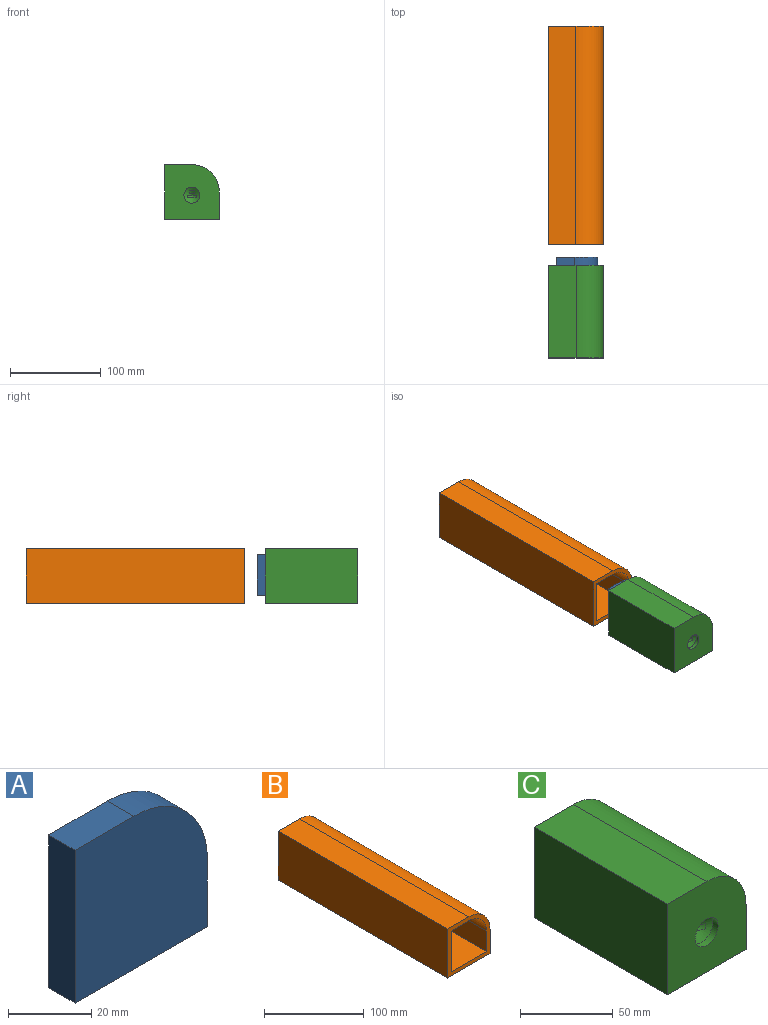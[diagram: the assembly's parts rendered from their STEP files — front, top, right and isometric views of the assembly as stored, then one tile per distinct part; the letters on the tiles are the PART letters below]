
ASSEMBLY  parts=3 mates=2
PART A: 7 faces, bbox 45x9x45 mm
  f0: plane 45x9mm, normal (-1,0,0), area 405mm2, adj f1,f4,f5,f6
  f1: plane 45x9mm, normal (0,0,-1), area 405mm2, adj f0,f2,f5,f6
  f2: plane 20x9mm, normal (1,0,0), area 180mm2, adj f1,f3,f5,f6
  f3: cylinder r=25mm len=25mm, axis (0,1,0), area 353.4mm2, adj f2,f4,f5,f6
  f4: plane 20x9mm, normal (0,0,1), area 180mm2, adj f0,f3,f5,f6
  f5: plane 45x45mm, normal (0,-1,0), area 1890.9mm2, adj f0,f1,f2,f3,f4
  f6: plane 45x45mm, normal (0,1,0), area 1890.9mm2, adj f0,f1,f2,f3,f4
PART B: 13 faces, bbox 60x240x60 mm
  f0: plane 60x60mm, normal (0,-1,0), area 1041mm2, adj f1,f2,f3,f4,f5,f7,f8,f9
  f1: plane 240x60mm, normal (-1,0,0), area 14400mm2, adj f0,f2,f5,f6
  f2: plane 240x60mm, normal (0,0,-1), area 14400mm2, adj f0,f1,f3,f6
  f3: plane 240x30mm, normal (1,0,0), area 7200mm2, adj f0,f2,f4,f6
  f4: cylinder r=30mm len=240mm, axis (0,1,0), area 11309.7mm2, adj f0,f3,f5,f6
  f5: plane 240x30mm, normal (0,0,1), area 7200mm2, adj f0,f1,f4,f6
  f6: plane 60x60mm, normal (0,1,0), area 3406.9mm2, adj f1,f2,f3,f4,f5
  f7: plane 235x50mm, normal (1,0,0), area 11750mm2, adj f0,f8,f11,f12
  f8: plane 235x50mm, normal (0,0,1), area 11750mm2, adj f0,f7,f9,f12
  f9: plane 235x25mm, normal (-1,0,0), area 5875mm2, adj f0,f8,f10,f12
  f10: cylinder r=25mm len=235mm, axis (0,1,0), area 9228.4mm2, adj f0,f9,f11,f12
  f11: plane 235x25mm, normal (0,0,-1), area 5875mm2, adj f0,f7,f10,f12
  f12: plane 50x50mm, normal (0,-1,0), area 2365.9mm2, adj f7,f8,f9,f10,f11
PART C: 19 faces, bbox 60x102x60 mm
  f0: plane 96.01x5mm, normal (0,0,-1), area 478.7mm2, adj f1,f3,f17,f18
  f1: plane 96.01x2.7mm, normal (-0.98,0,-0.18), area 261.9mm2, adj f0,f2,f3,f18
  f2: plane 94.99x6mm, normal (0,0,1), area 566.1mm2, adj f1,f3,f17,f18
  f3: plane 60x60mm, normal (0,1,0), area 3360.8mm2, adj f0,f1,f2,f4,f6,f7,f8,f9
  f4: plane 95.76x10.04mm, normal (0,0,-1), area 946.1mm2, adj f3,f5,f6,f8
  f5: cone r=0mm half-angle=59deg, axis (0,-1,0), area 36.4mm2, adj f4,f6,f7,f8
  f6: plane 96.29x3.11mm, normal (-1,0,0), area 298.1mm2, adj f3,f4,f5,f7
  f7: plane 96.29x10.04mm, normal (0,0,1), area 956.1mm2, adj f3,f5,f6,f8
  f8: plane 96.29x3.11mm, normal (1,0,0), area 298.1mm2, adj f3,f4,f5,f7
  f9: plane 102x60mm, normal (0,0,-1), area 6120mm2, adj f3,f10,f13,f16
  f10: plane 60x60mm, normal (0,-1,0), area 3166.3mm2, adj f9,f11,f13,f14,f15,f16
  f11: cylinder r=8.75mm len=17.5mm, axis (0,-1,0), area 219.9mm2, adj f10,f12
  f12: cone r=0mm half-angle=59deg, axis (0,-1,0), area 280.6mm2, adj f11
  f13: plane 102x30mm, normal (1,0,0), area 3060mm2, adj f3,f9,f10,f14
  f14: cylinder r=30mm len=102mm, axis (0,1,0), area 4806.6mm2, adj f3,f10,f13,f15
  f15: plane 102x30mm, normal (0,0,1), area 3060mm2, adj f3,f10,f14,f16
  f16: plane 102x60mm, normal (-1,0,0), area 6120mm2, adj f3,f9,f10,f15
  f17: plane 95.95x2.7mm, normal (0.98,0,-0.18), area 261.7mm2, adj f0,f2,f3,f18
  f18: cone r=0mm half-angle=59deg, axis (0,-1,0), area 17.3mm2, adj f0,f1,f2,f17
PLACE A t=(-6.41,-254.19,-1.3)mm
PLACE B at identity fixed
PLACE C t=(-0.14,-263.19,-15)mm
MATE slider B.f4 <-> A.f6  axis (0,-1,0) through (-30.14,-5,15)mm
MATE fastened A.f5 <-> C.f14  axis (0,-1,0) through (-30.14,-263.19,15)mm
